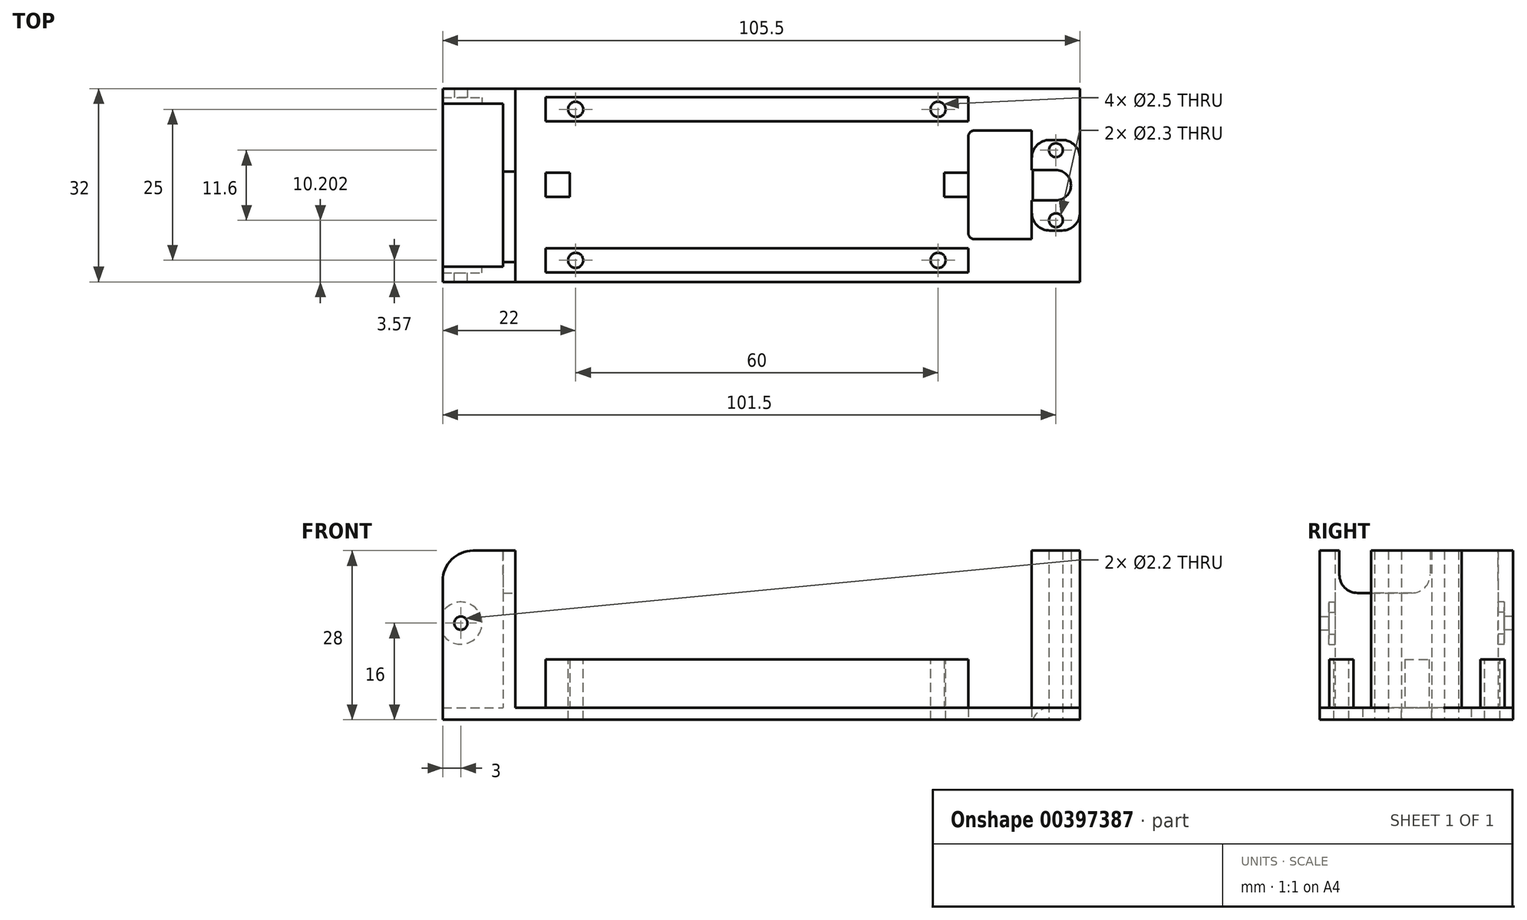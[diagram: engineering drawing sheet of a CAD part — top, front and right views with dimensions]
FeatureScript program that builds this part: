
annotation { "Feature Type Name" : "Feature", "Feature Type Description" : "" }
export const myFeature = defineFeature(function(context is Context, id is Id, definition is map)
    precondition{}
    {
        {
            var Q0;
            Q0=qCreatedBy(makeId("Top.planeOp"),FACE);
            var sketch = newSketch(context, id + "F0", { "sketchPlane" : qUnion([Q0])});
            skLineSegment(sketch, "E0.bottom", {"start": v(53.5, -16.07) * mm, "end": v(-52, -16.07) * mm});
            skLineSegment(sketch, "E0.top", {"start": v(53.5, 15.93) * mm, "end": v(-52, 15.93) * mm});
            skLineSegment(sketch, "E0.left", {"start": v(53.5, -16.07) * mm, "end": v(53.5, 15.93) * mm});
            skLineSegment(sketch, "E1", {"start": v(53.5, 7.43) * mm, "end": v(45.5, 7.43) * mm});
            skLineSegment(sketch, "E2", {"start": v(45.5, 7.43) * mm, "end": v(45.5, -7.57) * mm});
            skLineSegment(sketch, "E3", {"start": v(45.5, -7.57) * mm, "end": v(53.5, -7.57) * mm});
            skLineSegment(sketch, "E4", {"start": v(-52, 15.93) * mm, "end": v(-52, -16.07) * mm});
            skLineSegment(sketch, "E5.bottom", {"start": v(35, -10.5) * mm, "end": v(-35, -10.5) * mm});
            skLineSegment(sketch, "E5.top", {"start": v(35, 10.5) * mm, "end": v(-35, 10.5) * mm});
            skLineSegment(sketch, "E5.left", {"start": v(35, -10.5) * mm, "end": v(35, 10.5) * mm});
            skLineSegment(sketch, "E5.right", {"start": v(-35, -10.5) * mm, "end": v(-35, 10.5) * mm});
            skPoint(sketch, "E5.middle", {"position": v(0, 0) * mm});
            skLineSegment(sketch, "E6", {"start": v(45.5, 2.43) * mm, "end": v(49.5, 2.43) * mm});
            skPoint(sketch, "E6.endSnap0", {"position": v(49.5, 7.43) * mm});
            skLineSegment(sketch, "E7", {"start": v(45.5, -2.57) * mm, "end": v(49.5, -2.57) * mm});
            skArc(sketch, "E8", {"start": v(49.5, -2.57) * mm, "mid": v(52, -0.07) * mm, "end": v(49.5, 2.43) * mm});
            skPoint(sketch, "E9", {"position": v(53.5, -0.07) * mm});
            skLineSegment(sketch, "E10", {"start": v(-40, 15.93) * mm, "end": v(-40, -16.07) * mm});
            skLineSegment(sketch, "E11", {"start": v(-52, 13.43) * mm, "end": v(-42, 13.43) * mm});
            skLineSegment(sketch, "E12", {"start": v(-42, 13.43) * mm, "end": v(-42, -13.57) * mm});
            skLineSegment(sketch, "E13", {"start": v(-42, -13.57) * mm, "end": v(-52, -13.57) * mm});
            skLineSegment(sketch, "E14", {"start": v(-35, 10.5) * mm, "end": v(-35, 14.5) * mm});
            skLineSegment(sketch, "E15", {"start": v(-35, 14.5) * mm, "end": v(35, 14.5) * mm});
            skLineSegment(sketch, "E16", {"start": v(35, 14.5) * mm, "end": v(35, 10.5) * mm});
            skLineSegment(sketch, "E17", {"start": v(-35, -10.5) * mm, "end": v(-35, -14.5) * mm});
            skLineSegment(sketch, "E18", {"start": v(-35, -14.5) * mm, "end": v(35, -14.5) * mm});
            skLineSegment(sketch, "E19", {"start": v(35, -14.5) * mm, "end": v(35, -10.5) * mm});
            skLineSegment(sketch, "E20.bottom", {"start": v(-35, -2) * mm, "end": v(-31, -2) * mm});
            skLineSegment(sketch, "E20.top", {"start": v(-35, 2) * mm, "end": v(-31, 2) * mm});
            skLineSegment(sketch, "E20.left", {"start": v(-35, -2) * mm, "end": v(-35, 2) * mm});
            skLineSegment(sketch, "E20.right", {"start": v(-31, -2) * mm, "end": v(-31, 2) * mm});
            skPoint(sketch, "E20.middle", {"position": v(-33, 0) * mm});
            skLineSegment(sketch, "E21.bottom", {"start": v(35, -2) * mm, "end": v(31, -2) * mm});
            skLineSegment(sketch, "E21.top", {"start": v(35, 2) * mm, "end": v(31, 2) * mm});
            skLineSegment(sketch, "E21.left", {"start": v(35, -2) * mm, "end": v(35, 2) * mm});
            skLineSegment(sketch, "E21.right", {"start": v(31, -2) * mm, "end": v(31, 2) * mm});
            skPoint(sketch, "E21.middle", {"position": v(33, 0) * mm});
            skPoint(sketch, "E22", {"position": v(49.5, 5.73) * mm});
            skPoint(sketch, "E23", {"position": v(49.5, -5.87) * mm});
            skLineSegment(sketch, "E24", {"start": v(45.5, 9) * mm, "end": v(35, 9) * mm});
            skLineSegment(sketch, "E25", {"start": v(45.5, -9) * mm, "end": v(35, -9) * mm});
            skLineSegment(sketch, "E26", {"start": v(45.5, -9) * mm, "end": v(45.5, -7.57) * mm});
            skLineSegment(sketch, "E27", {"start": v(45.5, 7.43) * mm, "end": v(45.5, 9) * mm});
            skSolve(sketch);
        }
        {
            var Q0;
            {var subQ0=sQuery(id+"F0.wireOp",EDGE,"E11");Q0=makeQuery(id+"F0.imprint","IMPRINT",FACE,{"disambiguationData":[TD([[makeQuery(id+"F0.imprint","IMPRINT",EDGE,{"derivedFrom":subQ0}),-1.0]])]});}
            var Q1;
            {var subQ5=sQuery(id+"F0.wireOp",EDGE,"E1");Q1=makeQuery(id+"F0.imprint","IMPRINT",FACE,{"disambiguationData":[TD([[makeQuery(id+"F0.imprint","IMPRINT",EDGE,{"derivedFrom":subQ5}),-1.0]])]});}
            var Q2;
            {var subQ5=sQuery(id+"F0.wireOp",EDGE,"E5.bottom");Q2=makeQuery(id+"F0.imprint","IMPRINT",FACE,{"disambiguationData":[TD([[makeQuery(id+"F0.imprint","IMPRINT",EDGE,{"derivedFrom":subQ5}),-1.0]])]});}
            var Q3;
            {var subQ0=sQuery(id+"F0.wireOp",EDGE,"E6");Q3=makeQuery(id+"F0.imprint","IMPRINT",FACE,{"disambiguationData":[TD([[makeQuery(id+"F0.imprint","IMPRINT",EDGE,{"derivedFrom":subQ0}),-1.0]])]});}
            extrude(context, id + "F1", {"entities" : qUnion([Q0, Q1, Q2, Q3]), "depth" : 2 * mm});
        }
        {
            var Q0;
            Q0=makeQuery(id+"F0.imprint","IMPRINT",FACE,{"disambiguationData":[TD([[makeQuery(id+"F0.imprint","IMPRINT",EDGE,{"derivedFrom":sQuery(id+"F0.wireOp",EDGE,"E5.top")}),-1.0]])]});
            var Q1;
            Q1=makeQuery(id+"F0.imprint","IMPRINT",FACE,{"disambiguationData":[TD([[makeQuery(id+"F0.imprint","IMPRINT",EDGE,{"derivedFrom":sQuery(id+"F0.wireOp",EDGE,"E20.bottom")}),1.0]])]});
            var Q2;
            Q2=makeQuery(id+"F0.imprint","IMPRINT",FACE,{"disambiguationData":[TD([[makeQuery(id+"F0.imprint","IMPRINT",EDGE,{"derivedFrom":sQuery(id+"F0.wireOp",EDGE,"E5.bottom")}),1.0]])]});
            var Q3;
            Q3=makeQuery(id+"F0.imprint","IMPRINT",FACE,{"disambiguationData":[TD([[makeQuery(id+"F0.imprint","IMPRINT",EDGE,{"derivedFrom":sQuery(id+"F0.wireOp",EDGE,"E21.bottom")}),-1.0]])]});
            extrude(context, id + "F2", {"entities" : qUnion([Q0, Q1, Q2, Q3]), "operationType" : NewBodyOperationType.ADD, "depth" : 10 * mm});
        }
        {
            var Q0;
            {var subQ6=sQuery(id+"F0.wireOp",EDGE,"E10");Q0=makeQuery(id+"F0.imprint","IMPRINT",FACE,{"disambiguationData":[TD([[makeQuery(id+"F0.imprint","IMPRINT",EDGE,{"derivedFrom":subQ6}),-1.0]])]});}
            var Q1;
            {var subQ1=sQuery(id+"F0.wireOp",EDGE,"E1");Q1=makeQuery(id+"F0.imprint","IMPRINT",FACE,{"disambiguationData":[TD([[makeQuery(id+"F0.imprint","IMPRINT",EDGE,{"derivedFrom":subQ1}),1.0]])]});}
            extrude(context, id + "F3", {"entities" : qUnion([Q0, Q1]), "operationType" : NewBodyOperationType.ADD, "depth" : 28 * mm});
        }
        {
            var Q0;
            Q0=makeQuery(id+"F3.opExtrude","SWEPT_FACE",FACE,{"disambiguationData":[OSD([sQuery(id+"F0.wireOp",EDGE,"E10")])]});
            var sketch = newSketch(context, id + "F4", { "sketchPlane" : qUnion([Q0])});
            skLineSegment(sketch, "E28", {"start": v(-12.82, 28) * mm, "end": v(-12.82, 21) * mm});
            skLineSegment(sketch, "E29", {"start": v(-12.82, 21) * mm, "end": v(2.18, 21) * mm});
            skLineSegment(sketch, "E30", {"start": v(2.18, 21) * mm, "end": v(2.18, 28) * mm});
            skSolve(sketch);
        }
        {
            var Q0;
            {var subQ0=sQuery(id+"F4.wireOp",EDGE,"E28");Q0=makeQuery(id+"F4.imprint","IMPRINT",FACE,{"disambiguationData":[TD([[makeQuery(id+"F4.imprint","IMPRINT",EDGE,{"derivedFrom":subQ0}),1.0]])]});}
            extrude(context, id + "F5", {"entities" : qUnion([Q0]), "operationType" : NewBodyOperationType.REMOVE, "endBound" : BoundingType.UP_TO_NEXT, "oppositeDirection" : true, "depth" : 25 * mm});
        }
        {
            var Q0;
            Q0=makeQuery(id+"F1.opExtrude","CAP_EDGE",EDGE,{"disambiguationData":[OSD([sQuery(id+"F0.wireOp",EDGE,"E18")])],"isStart":false});
            var Q1;
            Q1=makeQuery(id+"F1.opExtrude","CAP_EDGE",EDGE,{"disambiguationData":[OSD([sQuery(id+"F0.wireOp",EDGE,"E15")])],"isStart":false});
            var Q2;
            Q2=makeQuery(id+"F1.opExtrude","CAP_EDGE",EDGE,{"disambiguationData":[OSD([sQuery(id+"F0.wireOp",EDGE,"E3")])],"isStart":false});
            var Q3;
            Q3=makeQuery(id+"F1.opExtrude","CAP_EDGE",EDGE,{"disambiguationData":[OSD([sQuery(id+"F0.wireOp",EDGE,"E1")])],"isStart":false});
            var Q4;
            {var subQ0=sQuery(id+"F0.wireOp",EDGE,"E4");Q4=makeQuery(id+"F3.opExtrude","CAP_EDGE",EDGE,{"disambiguationData":[OSD([subQ0]),TDD([makeQuery(id+"F0.imprint","IMPRINT",EDGE,{"disambiguationData":[TD([[makeQuery(id+"F0.imprint","INTERSECT",VERTEX,{"derivedFrom":[sQuery(id+"F0.wireOp",EDGE,"E0.top"),subQ0]}),-1.0]])],"derivedFrom":subQ0})])],"isStart":false});}
            var Q5;
            {var subQ0=sQuery(id+"F0.wireOp",EDGE,"E4");Q5=makeQuery(id+"F3.opExtrude","CAP_EDGE",EDGE,{"disambiguationData":[OSD([subQ0]),TDD([makeQuery(id+"F0.imprint","IMPRINT",EDGE,{"disambiguationData":[TD([[makeQuery(id+"F0.imprint","INTERSECT",VERTEX,{"derivedFrom":[sQuery(id+"F0.wireOp",EDGE,"E0.bottom"),subQ0]}),1.0]])],"derivedFrom":subQ0})])],"isStart":false});}
            fillet(context, id + "F6", {"entities" : qUnion([Q0, Q1, Q2, Q3, Q4, Q5]), "radius" : 5 * mm, "tangentPropagation" : true, "allowEdgeOverflow" : false});
        }
        {
            var Q0;
            Q0=makeQuery(id+"F1.opExtrude","CAP_EDGE",EDGE,{"disambiguationData":[OSD([sQuery(id+"F0.wireOp",EDGE,"E10")])],"isStart":false});
            var Q1;
            {var subQ0=sQuery(id+"F0.wireOp",EDGE,"E2");Q1=makeQuery(id+"F1.opExtrude","CAP_EDGE",EDGE,{"disambiguationData":[OSD([subQ0]),TDD([makeQuery(id+"F0.imprint","IMPRINT",EDGE,{"disambiguationData":[TD([[makeQuery(id+"F0.imprint","INTERSECT",VERTEX,{"derivedFrom":[subQ0,sQuery(id+"F0.wireOp",EDGE,"E3")]}),1.0]])],"derivedFrom":subQ0})])],"isStart":false});}
            var Q2;
            {var subQ0=sQuery(id+"F0.wireOp",EDGE,"E2");Q2=makeQuery(id+"F1.opExtrude","CAP_EDGE",EDGE,{"disambiguationData":[OSD([subQ0]),TDD([makeQuery(id+"F0.imprint","IMPRINT",EDGE,{"disambiguationData":[TD([[makeQuery(id+"F0.imprint","INTERSECT",VERTEX,{"derivedFrom":[sQuery(id+"F0.wireOp",EDGE,"E1"),subQ0]}),-1.0]])],"derivedFrom":subQ0})])],"isStart":false});}
            var Q3;
            Q3=makeQuery(id+"F3.opExtrude","SWEPT_EDGE",EDGE,{"disambiguationData":[OSD([sQuery(id+"F0.wireOp",EDGE,"E2"),sQuery(id+"F0.wireOp",EDGE,"E3")])]});
            var Q4;
            Q4=makeQuery(id+"F3.opExtrude","SWEPT_EDGE",EDGE,{"disambiguationData":[OSD([sQuery(id+"F0.wireOp",EDGE,"E0.left"),sQuery(id+"F0.wireOp",EDGE,"E3")])]});
            var Q5;
            Q5=makeQuery(id+"F3.opExtrude","SWEPT_EDGE",EDGE,{"disambiguationData":[OSD([sQuery(id+"F0.wireOp",EDGE,"E0.left"),sQuery(id+"F0.wireOp",EDGE,"E1")])]});
            var Q6;
            Q6=makeQuery(id+"F3.opExtrude","SWEPT_EDGE",EDGE,{"disambiguationData":[OSD([sQuery(id+"F0.wireOp",EDGE,"E1"),sQuery(id+"F0.wireOp",EDGE,"E2")])]});
            var Q7;
            Q7=makeQuery(id+"F1.opExtrude","CAP_EDGE",EDGE,{"disambiguationData":[OSD([sQuery(id+"F0.wireOp",EDGE,"E12")])],"isStart":false});
            var Q8;
            Q8=makeQuery(id+"F5.boolean.opBoolean","COPY",EDGE,{"derivedFrom":makeQuery(id+"F5.opExtrude","SWEPT_EDGE",EDGE,{"disambiguationData":[OSD([sQuery(id+"F4.wireOp",EDGE,"E28"),sQuery(id+"F4.wireOp",EDGE,"E29")])]})});
            var Q9;
            Q9=makeQuery(id+"F5.boolean.opBoolean","COPY",EDGE,{"derivedFrom":makeQuery(id+"F5.opExtrude","SWEPT_EDGE",EDGE,{"disambiguationData":[OSD([sQuery(id+"F4.wireOp",EDGE,"E29"),sQuery(id+"F4.wireOp",EDGE,"E30")])]})});
            fillet(context, id + "F7", {"entities" : qUnion([Q0, Q1, Q2, Q3, Q4, Q5, Q6, Q7, Q8, Q9]), "radius" : 3 * mm, "tangentPropagation" : true, "allowEdgeOverflow" : false});
        }
        {
            var Q0;
            Q0=sQuery(id+"F0.wireOp",VERTEX,"E22");
            var Q1;
            Q1=sQuery(id+"F0.wireOp",VERTEX,"E23");
            var Q2;
            Q2=makeQuery(id+"F1.opExtrude","SWEPT_BODY",BODY,{"disambiguationData":[OSD([sQuery(id+"F0.wireOp",EDGE,"E0.bottom"),sQuery(id+"F0.wireOp",EDGE,"E0.top"),sQuery(id+"F0.wireOp",EDGE,"E0.left"),sQuery(id+"F0.wireOp",EDGE,"E1"),sQuery(id+"F0.wireOp",EDGE,"E2"),sQuery(id+"F0.wireOp",EDGE,"E3"),sQuery(id+"F0.wireOp",EDGE,"E5.bottom"),sQuery(id+"F0.wireOp",EDGE,"E5.top"),sQuery(id+"F0.wireOp",EDGE,"E6"),sQuery(id+"F0.wireOp",EDGE,"E7"),sQuery(id+"F0.wireOp",EDGE,"E8"),sQuery(id+"F0.wireOp",EDGE,"E10"),sQuery(id+"F0.wireOp",EDGE,"E14"),sQuery(id+"F0.wireOp",EDGE,"E15"),sQuery(id+"F0.wireOp",EDGE,"E16"),sQuery(id+"F0.wireOp",EDGE,"E17"),sQuery(id+"F0.wireOp",EDGE,"E18"),sQuery(id+"F0.wireOp",EDGE,"E19"),sQuery(id+"F0.wireOp",EDGE,"E20.bottom"),sQuery(id+"F0.wireOp",EDGE,"E20.top"),sQuery(id+"F0.wireOp",EDGE,"E20.left"),sQuery(id+"F0.wireOp",EDGE,"E20.right"),sQuery(id+"F0.wireOp",EDGE,"E21.bottom"),sQuery(id+"F0.wireOp",EDGE,"E21.top"),sQuery(id+"F0.wireOp",EDGE,"E21.left"),sQuery(id+"F0.wireOp",EDGE,"E21.right")])]});
            hole(context, id + "F8", {"style" : HoleStyle.SIMPLE, "endStyle" : HoleEndStyle.THROUGH, "oppositeDirection" : true, "holeDiameter" : 2.3 * mm, "isTappedThrough" : true, "tappedDepth" : 12 * mm, "tapClearance" : 3, "locations" : qUnion([Q0, Q1]), "scope" : qUnion([Q2])});
        }
        {
            var Q0;
            Q0=makeQuery(id+"F3.opExtrude","SWEPT_FACE",FACE,{"disambiguationData":[OSD([sQuery(id+"F0.wireOp",EDGE,"E11")])]});
            var sketch = newSketch(context, id + "F9", { "sketchPlane" : qUnion([Q0])});
            skPoint(sketch, "E31", {"position": v(-49, 16) * mm});
            skCircle(sketch, "E32", {"center": v(-49, 16) * mm, "radius": 3.5 * mm});
            skSolve(sketch);
        }
        {
            var Q0;
            {var subQ0=sQuery(id+"F9.wireOp",EDGE,"E32");var subQ1=makeQuery(id+"F3.opExtrude","SWEPT_EDGE",EDGE,{"disambiguationData":[OSD([sQuery(id+"F0.wireOp",EDGE,"E4"),sQuery(id+"F0.wireOp",EDGE,"E11")])]});var subQ2=makeQuery(id+"F9.imprint","INTERSECT",VERTEX,{"disambiguationData":[OD(0.0)],"derivedFrom":[subQ1,subQ0]});Q0=makeQuery(id+"F9.imprint","IMPRINT",FACE,{"disambiguationData":[TD([[makeQuery(id+"F9.imprint","IMPRINT",EDGE,{"disambiguationData":[TD([[subQ2,-1.0]])],"derivedFrom":subQ0}),1.0]])]});}
            extrude(context, id + "F10", {"entities" : qUnion([Q0]), "operationType" : NewBodyOperationType.REMOVE, "oppositeDirection" : true, "depth" : 1 * mm});
        }
        {
            var Q0;
            Q0=sQuery(id+"F9.wireOp",VERTEX,"E31");
            var Q1;
            Q1=makeQuery(id+"F1.opExtrude","SWEPT_BODY",BODY,{"disambiguationData":[OSD([sQuery(id+"F0.wireOp",EDGE,"E0.bottom"),sQuery(id+"F0.wireOp",EDGE,"E0.top"),sQuery(id+"F0.wireOp",EDGE,"E0.left"),sQuery(id+"F0.wireOp",EDGE,"E1"),sQuery(id+"F0.wireOp",EDGE,"E2"),sQuery(id+"F0.wireOp",EDGE,"E3"),sQuery(id+"F0.wireOp",EDGE,"E5.bottom"),sQuery(id+"F0.wireOp",EDGE,"E5.top"),sQuery(id+"F0.wireOp",EDGE,"E6"),sQuery(id+"F0.wireOp",EDGE,"E7"),sQuery(id+"F0.wireOp",EDGE,"E8"),sQuery(id+"F0.wireOp",EDGE,"E10"),sQuery(id+"F0.wireOp",EDGE,"E14"),sQuery(id+"F0.wireOp",EDGE,"E15"),sQuery(id+"F0.wireOp",EDGE,"E16"),sQuery(id+"F0.wireOp",EDGE,"E17"),sQuery(id+"F0.wireOp",EDGE,"E18"),sQuery(id+"F0.wireOp",EDGE,"E19"),sQuery(id+"F0.wireOp",EDGE,"E20.bottom"),sQuery(id+"F0.wireOp",EDGE,"E20.top"),sQuery(id+"F0.wireOp",EDGE,"E20.left"),sQuery(id+"F0.wireOp",EDGE,"E20.right"),sQuery(id+"F0.wireOp",EDGE,"E21.bottom"),sQuery(id+"F0.wireOp",EDGE,"E21.top"),sQuery(id+"F0.wireOp",EDGE,"E21.left"),sQuery(id+"F0.wireOp",EDGE,"E21.right")])]});
            hole(context, id + "F11", {"style" : HoleStyle.SIMPLE, "endStyle" : HoleEndStyle.THROUGH, "holeDiameter" : 2.2 * mm, "isTappedThrough" : true, "tappedDepth" : 12 * mm, "tapClearance" : 3, "locations" : qUnion([Q0]), "scope" : qUnion([Q1])});
        }
        {
            var Q0;
            Q0=makeQuery(id+"F3.opExtrude","SWEPT_FACE",FACE,{"disambiguationData":[OSD([sQuery(id+"F0.wireOp",EDGE,"E13")])]});
            var sketch = newSketch(context, id + "F12", { "sketchPlane" : qUnion([Q0])});
            skPoint(sketch, "E33", {"position": v(49, 16) * mm});
            skCircle(sketch, "E34", {"center": v(49, 16) * mm, "radius": 3.5 * mm});
            skSolve(sketch);
        }
        {
            var Q0;
            {var subQ0=sQuery(id+"F12.wireOp",EDGE,"E34");var subQ1=makeQuery(id+"F3.opExtrude","SWEPT_EDGE",EDGE,{"disambiguationData":[OSD([sQuery(id+"F0.wireOp",EDGE,"E4"),sQuery(id+"F0.wireOp",EDGE,"E13")])]});var subQ2=makeQuery(id+"F12.imprint","INTERSECT",VERTEX,{"disambiguationData":[OD(0.0)],"derivedFrom":[subQ1,subQ0]});Q0=makeQuery(id+"F12.imprint","IMPRINT",FACE,{"disambiguationData":[TD([[makeQuery(id+"F12.imprint","IMPRINT",EDGE,{"disambiguationData":[TD([[subQ2,1.0]])],"derivedFrom":subQ0}),1.0]])]});}
            extrude(context, id + "F13", {"entities" : qUnion([Q0]), "operationType" : NewBodyOperationType.REMOVE, "oppositeDirection" : true, "depth" : 1 * mm});
        }
        {
            var Q0;
            Q0=sQuery(id+"F12.wireOp",VERTEX,"E33");
            var Q1;
            Q1=makeQuery(id+"F1.opExtrude","SWEPT_BODY",BODY,{"disambiguationData":[OSD([sQuery(id+"F0.wireOp",EDGE,"E0.bottom"),sQuery(id+"F0.wireOp",EDGE,"E0.top"),sQuery(id+"F0.wireOp",EDGE,"E0.left"),sQuery(id+"F0.wireOp",EDGE,"E1"),sQuery(id+"F0.wireOp",EDGE,"E2"),sQuery(id+"F0.wireOp",EDGE,"E3"),sQuery(id+"F0.wireOp",EDGE,"E5.bottom"),sQuery(id+"F0.wireOp",EDGE,"E5.top"),sQuery(id+"F0.wireOp",EDGE,"E6"),sQuery(id+"F0.wireOp",EDGE,"E7"),sQuery(id+"F0.wireOp",EDGE,"E8"),sQuery(id+"F0.wireOp",EDGE,"E10"),sQuery(id+"F0.wireOp",EDGE,"E14"),sQuery(id+"F0.wireOp",EDGE,"E15"),sQuery(id+"F0.wireOp",EDGE,"E16"),sQuery(id+"F0.wireOp",EDGE,"E17"),sQuery(id+"F0.wireOp",EDGE,"E18"),sQuery(id+"F0.wireOp",EDGE,"E19"),sQuery(id+"F0.wireOp",EDGE,"E20.bottom"),sQuery(id+"F0.wireOp",EDGE,"E20.top"),sQuery(id+"F0.wireOp",EDGE,"E20.left"),sQuery(id+"F0.wireOp",EDGE,"E20.right"),sQuery(id+"F0.wireOp",EDGE,"E21.bottom"),sQuery(id+"F0.wireOp",EDGE,"E21.top"),sQuery(id+"F0.wireOp",EDGE,"E21.left"),sQuery(id+"F0.wireOp",EDGE,"E21.right")])]});
            hole(context, id + "F14", {"style" : HoleStyle.SIMPLE, "endStyle" : HoleEndStyle.THROUGH, "holeDiameter" : 2.2 * mm, "isTappedThrough" : true, "tappedDepth" : 12 * mm, "tapClearance" : 3, "locations" : qUnion([Q0]), "scope" : qUnion([Q1])});
        }
        {
            var Q0;
            Q0=makeQuery(id+"F1.opExtrude","SWEPT_EDGE",EDGE,{"disambiguationData":[OSD([sQuery(id+"F0.wireOp",EDGE,"E5.left"),sQuery(id+"F0.wireOp",EDGE,"E24")])]});
            var Q1;
            Q1=makeQuery(id+"F1.opExtrude","SWEPT_EDGE",EDGE,{"disambiguationData":[OSD([sQuery(id+"F0.wireOp",EDGE,"E5.left"),sQuery(id+"F0.wireOp",EDGE,"E25")])]});
            var Q2;
            {var subQ0=sQuery(id+"F0.wireOp",EDGE,"E26");var subQ1=sQuery(id+"F0.wireOp",EDGE,"E3");var subQ2=sQuery(id+"F0.wireOp",EDGE,"E2");var subQ3=sQuery(id+"F0.wireOp",EDGE,"E27");Q2=makeQuery(id+"F7.opFillet","BLEND_EDGE",EDGE,{"blendedFrom":[makeQuery(id+"F6.opFillet","BLEND_EDGE",EDGE,{"blendedFrom":[makeQuery(id+"F1.opExtrude","CAP_EDGE",EDGE,{"disambiguationData":[OSD([subQ1])],"isStart":false}),makeQuery(id+"F3.boolean.opBoolean","MERGE",FACE,{"derivedFrom":[makeQuery(id+"F1.opExtrude","SWEPT_FACE",FACE,{"disambiguationData":[OSD([subQ2])]}),makeQuery(id+"F1.opExtrude","SWEPT_FACE",FACE,{"disambiguationData":[OSD([subQ0])]}),makeQuery(id+"F1.opExtrude","SWEPT_FACE",FACE,{"disambiguationData":[OSD([subQ3])]}),makeQuery(id+"F3.opExtrude","SWEPT_FACE",FACE,{"disambiguationData":[OSD([subQ2]),TDD([makeQuery(id+"F0.imprint","IMPRINT",EDGE,{"disambiguationData":[TD([[makeQuery(id+"F0.imprint","INTERSECT",VERTEX,{"derivedFrom":[subQ2,sQuery(id+"F0.wireOp",EDGE,"E6")]}),1.0]])],"derivedFrom":subQ2})])]}),makeQuery(id+"F3.opExtrude","SWEPT_FACE",FACE,{"disambiguationData":[OSD([subQ2]),TDD([makeQuery(id+"F0.imprint","IMPRINT",EDGE,{"disambiguationData":[TD([[makeQuery(id+"F0.imprint","INTERSECT",VERTEX,{"derivedFrom":[subQ2,sQuery(id+"F0.wireOp",EDGE,"E7")]}),-1.0]])],"derivedFrom":subQ2})])]})]})],"blendedInto":[makeQuery(id+"F3.boolean.opBoolean","MERGE",FACE,{"derivedFrom":[makeQuery(id+"F1.opExtrude","SWEPT_FACE",FACE,{"disambiguationData":[OSD([subQ2])]}),makeQuery(id+"F1.opExtrude","SWEPT_FACE",FACE,{"disambiguationData":[OSD([subQ0])]}),makeQuery(id+"F1.opExtrude","SWEPT_FACE",FACE,{"disambiguationData":[OSD([subQ3])]}),makeQuery(id+"F3.opExtrude","SWEPT_FACE",FACE,{"disambiguationData":[OSD([subQ2]),TDD([makeQuery(id+"F0.imprint","IMPRINT",EDGE,{"disambiguationData":[TD([[makeQuery(id+"F0.imprint","INTERSECT",VERTEX,{"derivedFrom":[subQ2,sQuery(id+"F0.wireOp",EDGE,"E6")]}),1.0]])],"derivedFrom":subQ2})])]}),makeQuery(id+"F3.opExtrude","SWEPT_FACE",FACE,{"disambiguationData":[OSD([subQ2]),TDD([makeQuery(id+"F0.imprint","IMPRINT",EDGE,{"disambiguationData":[TD([[makeQuery(id+"F0.imprint","INTERSECT",VERTEX,{"derivedFrom":[subQ2,sQuery(id+"F0.wireOp",EDGE,"E7")]}),-1.0]])],"derivedFrom":subQ2})])]})]})]}),makeQuery(id+"F1.opExtrude","SWEPT_FACE",FACE,{"disambiguationData":[OSD([sQuery(id+"F0.wireOp",EDGE,"E25")])]})],"blendedInto":[makeQuery(id+"F1.opExtrude","SWEPT_FACE",FACE,{"disambiguationData":[OSD([sQuery(id+"F0.wireOp",EDGE,"E25")])]})]});}
            var Q3;
            {var subQ0=sQuery(id+"F0.wireOp",EDGE,"E26");var subQ1=sQuery(id+"F0.wireOp",EDGE,"E2");var subQ2=sQuery(id+"F0.wireOp",EDGE,"E27");var subQ3=sQuery(id+"F0.wireOp",EDGE,"E1");Q3=makeQuery(id+"F7.opFillet","BLEND_EDGE",EDGE,{"blendedFrom":[makeQuery(id+"F6.opFillet","BLEND_EDGE",EDGE,{"blendedFrom":[makeQuery(id+"F1.opExtrude","CAP_EDGE",EDGE,{"disambiguationData":[OSD([subQ3])],"isStart":false}),makeQuery(id+"F3.boolean.opBoolean","MERGE",FACE,{"derivedFrom":[makeQuery(id+"F1.opExtrude","SWEPT_FACE",FACE,{"disambiguationData":[OSD([subQ1])]}),makeQuery(id+"F1.opExtrude","SWEPT_FACE",FACE,{"disambiguationData":[OSD([subQ0])]}),makeQuery(id+"F1.opExtrude","SWEPT_FACE",FACE,{"disambiguationData":[OSD([subQ2])]}),makeQuery(id+"F3.opExtrude","SWEPT_FACE",FACE,{"disambiguationData":[OSD([subQ1]),TDD([makeQuery(id+"F0.imprint","IMPRINT",EDGE,{"disambiguationData":[TD([[makeQuery(id+"F0.imprint","INTERSECT",VERTEX,{"derivedFrom":[subQ1,sQuery(id+"F0.wireOp",EDGE,"E6")]}),1.0]])],"derivedFrom":subQ1})])]}),makeQuery(id+"F3.opExtrude","SWEPT_FACE",FACE,{"disambiguationData":[OSD([subQ1]),TDD([makeQuery(id+"F0.imprint","IMPRINT",EDGE,{"disambiguationData":[TD([[makeQuery(id+"F0.imprint","INTERSECT",VERTEX,{"derivedFrom":[subQ1,sQuery(id+"F0.wireOp",EDGE,"E7")]}),-1.0]])],"derivedFrom":subQ1})])]})]})],"blendedInto":[makeQuery(id+"F3.boolean.opBoolean","MERGE",FACE,{"derivedFrom":[makeQuery(id+"F1.opExtrude","SWEPT_FACE",FACE,{"disambiguationData":[OSD([subQ1])]}),makeQuery(id+"F1.opExtrude","SWEPT_FACE",FACE,{"disambiguationData":[OSD([subQ0])]}),makeQuery(id+"F1.opExtrude","SWEPT_FACE",FACE,{"disambiguationData":[OSD([subQ2])]}),makeQuery(id+"F3.opExtrude","SWEPT_FACE",FACE,{"disambiguationData":[OSD([subQ1]),TDD([makeQuery(id+"F0.imprint","IMPRINT",EDGE,{"disambiguationData":[TD([[makeQuery(id+"F0.imprint","INTERSECT",VERTEX,{"derivedFrom":[subQ1,sQuery(id+"F0.wireOp",EDGE,"E6")]}),1.0]])],"derivedFrom":subQ1})])]}),makeQuery(id+"F3.opExtrude","SWEPT_FACE",FACE,{"disambiguationData":[OSD([subQ1]),TDD([makeQuery(id+"F0.imprint","IMPRINT",EDGE,{"disambiguationData":[TD([[makeQuery(id+"F0.imprint","INTERSECT",VERTEX,{"derivedFrom":[subQ1,sQuery(id+"F0.wireOp",EDGE,"E7")]}),-1.0]])],"derivedFrom":subQ1})])]})]})]}),makeQuery(id+"F1.opExtrude","SWEPT_FACE",FACE,{"disambiguationData":[OSD([sQuery(id+"F0.wireOp",EDGE,"E24")])]})],"blendedInto":[makeQuery(id+"F1.opExtrude","SWEPT_FACE",FACE,{"disambiguationData":[OSD([sQuery(id+"F0.wireOp",EDGE,"E24")])]})]});}
            var Q4;
            Q4=makeQuery(id+"F1.opExtrude","CAP_EDGE",EDGE,{"disambiguationData":[OSD([sQuery(id+"F0.wireOp",EDGE,"E8")])],"isStart":false});
            var Q5;
            Q5=makeQuery(id+"F1.opExtrude","CAP_EDGE",EDGE,{"disambiguationData":[OSD([sQuery(id+"F0.wireOp",EDGE,"E21.bottom")])],"isStart":false});
            var Q6;
            Q6=makeQuery(id+"F1.opExtrude","CAP_EDGE",EDGE,{"disambiguationData":[OSD([sQuery(id+"F0.wireOp",EDGE,"E21.right")])],"isStart":false});
            var Q7;
            Q7=makeQuery(id+"F1.opExtrude","CAP_EDGE",EDGE,{"disambiguationData":[OSD([sQuery(id+"F0.wireOp",EDGE,"E21.top")])],"isStart":false});
            var Q8;
            Q8=makeQuery(id+"F1.opExtrude","CAP_EDGE",EDGE,{"disambiguationData":[OSD([sQuery(id+"F0.wireOp",EDGE,"E20.right")])],"isStart":false});
            var Q9;
            Q9=makeQuery(id+"F1.opExtrude","CAP_EDGE",EDGE,{"disambiguationData":[OSD([sQuery(id+"F0.wireOp",EDGE,"E20.top")])],"isStart":false});
            var Q10;
            Q10=makeQuery(id+"F1.opExtrude","CAP_EDGE",EDGE,{"disambiguationData":[OSD([sQuery(id+"F0.wireOp",EDGE,"E20.bottom")])],"isStart":false});
            var Q11;
            Q11=makeQuery(id+"F1.opExtrude","CAP_EDGE",EDGE,{"disambiguationData":[OSD([sQuery(id+"F0.wireOp",EDGE,"E5.top")])],"isStart":false});
            var Q12;
            Q12=makeQuery(id+"F1.opExtrude","CAP_EDGE",EDGE,{"disambiguationData":[OSD([sQuery(id+"F0.wireOp",EDGE,"E5.bottom")])],"isStart":false});
            var Q13;
            Q13=makeQuery(id+"F1.opExtrude","CAP_EDGE",EDGE,{"disambiguationData":[OSD([sQuery(id+"F0.wireOp",EDGE,"E17")])],"isStart":false});
            var Q14;
            Q14=makeQuery(id+"F1.opExtrude","CAP_EDGE",EDGE,{"disambiguationData":[OSD([sQuery(id+"F0.wireOp",EDGE,"E14")])],"isStart":false});
            var Q15;
            Q15=makeQuery(id+"F1.opExtrude","CAP_EDGE",EDGE,{"disambiguationData":[OSD([sQuery(id+"F0.wireOp",EDGE,"E16")])],"isStart":false});
            var Q16;
            Q16=makeQuery(id+"F1.opExtrude","CAP_EDGE",EDGE,{"disambiguationData":[OSD([sQuery(id+"F0.wireOp",EDGE,"E19")])],"isStart":false});
            var Q17;
            Q17=makeQuery(id+"F1.opExtrude","CAP_EDGE",EDGE,{"disambiguationData":[OSD([sQuery(id+"F0.wireOp",EDGE,"E20.left")])],"isStart":false});
            fillet(context, id + "F15", {"entities" : qUnion([Q0, Q1, Q2, Q3, Q4, Q5, Q6, Q7, Q8, Q9, Q10, Q11, Q12, Q13, Q14, Q15, Q16, Q17]), "radius" : 1 * mm, "tangentPropagation" : true, "allowEdgeOverflow" : false});
        }
        {
            var Q0;
            Q0=makeQuery(id+"F2.opExtrude","CAP_FACE",FACE,{"disambiguationData":[OSD([sQuery(id+"F0.wireOp",EDGE,"E5.top"),sQuery(id+"F0.wireOp",EDGE,"E14"),sQuery(id+"F0.wireOp",EDGE,"E15"),sQuery(id+"F0.wireOp",EDGE,"E16")])],"isStart":false});
            var sketch = newSketch(context, id + "F16", { "sketchPlane" : qUnion([Q0])});
            skPoint(sketch, "E35", {"position": v(-30, 12.5) * mm});
            skPoint(sketch, "E35.positionSnap0", {"position": v(-35, 12.5) * mm});
            skPoint(sketch, "E36", {"position": v(30, 12.5) * mm});
            skPoint(sketch, "E36.positionSnap0", {"position": v(35, 12.5) * mm});
            skSolve(sketch);
        }
        {
            var Q0;
            Q0=makeQuery(id+"F2.opExtrude","CAP_FACE",FACE,{"disambiguationData":[OSD([sQuery(id+"F0.wireOp",EDGE,"E5.bottom"),sQuery(id+"F0.wireOp",EDGE,"E17"),sQuery(id+"F0.wireOp",EDGE,"E18"),sQuery(id+"F0.wireOp",EDGE,"E19")])],"isStart":false});
            var sketch = newSketch(context, id + "F17", { "sketchPlane" : qUnion([Q0])});
            skPoint(sketch, "E37", {"position": v(-30, -12.5) * mm});
            skPoint(sketch, "E37.positionSnap0", {"position": v(-35, -12.5) * mm});
            skPoint(sketch, "E38", {"position": v(30, -12.5) * mm});
            skPoint(sketch, "E38.positionSnap0", {"position": v(35, -12.5) * mm});
            skSolve(sketch);
        }
        {
            var Q0;
            Q0=sQuery(id+"F16.wireOp",VERTEX,"E35");
            var Q1;
            Q1=sQuery(id+"F17.wireOp",VERTEX,"E37");
            var Q2;
            Q2=sQuery(id+"F16.wireOp",VERTEX,"E36");
            var Q3;
            Q3=sQuery(id+"F17.wireOp",VERTEX,"E38");
            var Q4;
            Q4=makeQuery(id+"F1.opExtrude","SWEPT_BODY",BODY,{"disambiguationData":[OSD([sQuery(id+"F0.wireOp",EDGE,"E0.bottom"),sQuery(id+"F0.wireOp",EDGE,"E0.top"),sQuery(id+"F0.wireOp",EDGE,"E0.left"),sQuery(id+"F0.wireOp",EDGE,"E1"),sQuery(id+"F0.wireOp",EDGE,"E3"),sQuery(id+"F0.wireOp",EDGE,"E5.bottom"),sQuery(id+"F0.wireOp",EDGE,"E5.top"),sQuery(id+"F0.wireOp",EDGE,"E5.left"),sQuery(id+"F0.wireOp",EDGE,"E10"),sQuery(id+"F0.wireOp",EDGE,"E14"),sQuery(id+"F0.wireOp",EDGE,"E15"),sQuery(id+"F0.wireOp",EDGE,"E16"),sQuery(id+"F0.wireOp",EDGE,"E17"),sQuery(id+"F0.wireOp",EDGE,"E18"),sQuery(id+"F0.wireOp",EDGE,"E19"),sQuery(id+"F0.wireOp",EDGE,"E20.bottom"),sQuery(id+"F0.wireOp",EDGE,"E20.top"),sQuery(id+"F0.wireOp",EDGE,"E20.left"),sQuery(id+"F0.wireOp",EDGE,"E20.right"),sQuery(id+"F0.wireOp",EDGE,"E21.bottom"),sQuery(id+"F0.wireOp",EDGE,"E21.top"),sQuery(id+"F0.wireOp",EDGE,"E21.right"),sQuery(id+"F0.wireOp",EDGE,"E24"),sQuery(id+"F0.wireOp",EDGE,"E25"),sQuery(id+"F0.wireOp",EDGE,"E26"),sQuery(id+"F0.wireOp",EDGE,"E27")])]});
            hole(context, id + "F18", {"style" : HoleStyle.SIMPLE, "endStyle" : HoleEndStyle.BLIND, "holeDiameter" : 2.5 * mm, "holeDepth" : 20 * mm, "isTappedThrough" : true, "tappedDepth" : 12 * mm, "tapClearance" : 3, "locations" : qUnion([Q0, Q1, Q2, Q3]), "scope" : qUnion([Q4])});
        }
    });
